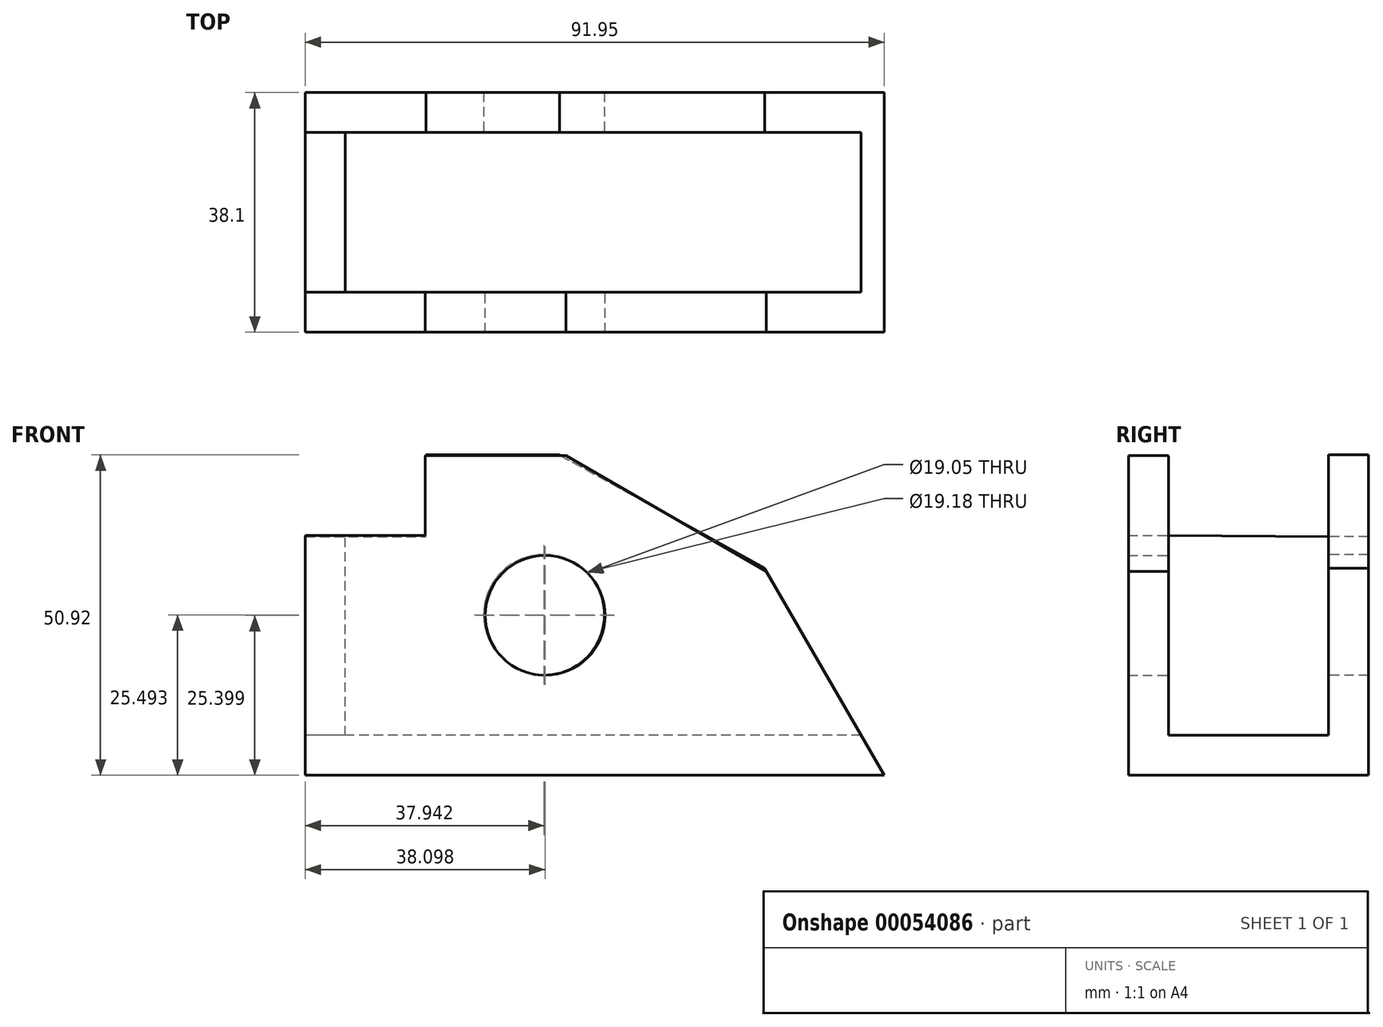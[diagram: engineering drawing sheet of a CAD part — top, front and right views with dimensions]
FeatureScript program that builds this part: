
annotation { "Feature Type Name" : "Feature", "Feature Type Description" : "" }
export const myFeature = defineFeature(function(context is Context, id is Id, definition is map)
    precondition{}
    {
        {
            var Q0;
            Q0=qCreatedBy(makeId("Front.planeOp"),FACE);
            var sketch = newSketch(context, id + "F0", { "sketchPlane" : qUnion([Q0])});
            skLineSegment(sketch, "E0", {"start": v(-65.28, -20.72) * mm, "end": v(26.67, -20.72) * mm});
            skLineSegment(sketch, "E1", {"start": v(-65.28, -20.72) * mm, "end": v(-65.28, 17.38) * mm});
            skLineSegment(sketch, "E2", {"start": v(-65.28, 17.38) * mm, "end": v(-46.23, 17.38) * mm});
            skLineSegment(sketch, "E3", {"start": v(-46.23, 17.38) * mm, "end": v(-46.23, 30.08) * mm});
            skLineSegment(sketch, "E4", {"start": v(-46.23, 30.08) * mm, "end": v(-23.88, 30.08) * mm});
            skLineSegment(sketch, "E5", {"start": v(7.95, 11.7) * mm, "end": v(-23.88, 30.08) * mm});
            skLineSegment(sketch, "E6", {"start": v(7.95, 11.7) * mm, "end": v(26.67, -20.72) * mm});
            skCircle(sketch, "E7", {"center": v(-27.18, 4.68) * mm, "radius": 9.53 * mm});
            skSolve(sketch);
        }
        {
            var Q0;
            Q0 = qSketchRegion(id + "F0", true);
            extrude(context, id + "F1", {"entities" : qUnion([Q0]), "depth" : 6.35 * mm});
        }
        {
            var Q0;
            Q0=makeQuery(id+"F1.opExtrude","CAP_FACE",FACE,{"disambiguationData":[OSD([sQuery(id+"F0.wireOp",EDGE,"E0"),sQuery(id+"F0.wireOp",EDGE,"E1"),sQuery(id+"F0.wireOp",EDGE,"E2"),sQuery(id+"F0.wireOp",EDGE,"E3"),sQuery(id+"F0.wireOp",EDGE,"E4"),sQuery(id+"F0.wireOp",EDGE,"E5"),sQuery(id+"F0.wireOp",EDGE,"E6"),sQuery(id+"F0.wireOp",EDGE,"E7")])],"isStart":true});
            var sketch = newSketch(context, id + "F2", { "sketchPlane" : qUnion([Q0])});
            skLineSegment(sketch, "E8", {"start": v(-26.67, -20.72) * mm, "end": v(-23, -14.37) * mm});
            skLineSegment(sketch, "E9", {"start": v(-23, -14.37) * mm, "end": v(65.28, -14.37) * mm});
            skLineSegment(sketch, "E10", {"start": v(65.28, -14.37) * mm, "end": v(65.28, -20.72) * mm});
            skLineSegment(sketch, "E11", {"start": v(65.28, -20.72) * mm, "end": v(-26.67, -20.72) * mm});
            skSolve(sketch);
        }
        {
            var Q0;
            Q0=makeQuery(id+"F2.imprint","IMPRINT",FACE,{"disambiguationData":[TD([[makeQuery(id+"F2.imprint","IMPRINT",EDGE,{"derivedFrom":sQuery(id+"F2.wireOp",EDGE,"E8")}),1.0]])]});
            extrude(context, id + "F3", {"entities" : qUnion([Q0]), "operationType" : NewBodyOperationType.ADD, "depth" : 25.4 * mm});
        }
        {
            var Q0;
            Q0=makeQuery(id+"F3.opExtrude","CAP_FACE",FACE,{"disambiguationData":[OSD([sQuery(id+"F2.wireOp",EDGE,"E8"),sQuery(id+"F2.wireOp",EDGE,"E9"),sQuery(id+"F2.wireOp",EDGE,"E10"),sQuery(id+"F2.wireOp",EDGE,"E11")])],"isStart":false});
            var sketch = newSketch(context, id + "F4", { "sketchPlane" : qUnion([Q0])});
            skLineSegment(sketch, "E12", {"start": v(-26.67, -20.72) * mm, "end": v(65.28, -20.72) * mm});
            skLineSegment(sketch, "E13", {"start": v(65.28, -20.72) * mm, "end": v(65.28, 17.22) * mm});
            skLineSegment(sketch, "E14", {"start": v(65.28, 17.22) * mm, "end": v(46.1, 17.22) * mm});
            skLineSegment(sketch, "E15", {"start": v(46.1, 17.22) * mm, "end": v(46.1, 30.2) * mm});
            skLineSegment(sketch, "E16", {"start": v(46.1, 30.2) * mm, "end": v(24.9, 30.2) * mm});
            skLineSegment(sketch, "E17", {"start": v(24.9, 30.2) * mm, "end": v(-7.68, 12.18) * mm});
            skLineSegment(sketch, "E18", {"start": v(-7.68, 12.18) * mm, "end": v(-26.67, -20.72) * mm});
            skCircle(sketch, "E19", {"center": v(27.34, 4.77) * mm, "radius": 9.6 * mm});
            skSolve(sketch);
        }
        {
            var Q0;
            Q0 = qSketchRegion(id + "F4", true);
            extrude(context, id + "F5", {"entities" : qUnion([Q0]), "operationType" : NewBodyOperationType.ADD, "depth" : 6.35 * mm});
        }
        {
            var Q0;
            Q0=makeQuery(id+"F5.boolean.opBoolean","MERGE",FACE,{"derivedFrom":[makeQuery(id+"F3.boolean.opBoolean","MERGE",FACE,{"derivedFrom":[makeQuery(id+"F1.opExtrude","SWEPT_FACE",FACE,{"disambiguationData":[OSD([sQuery(id+"F0.wireOp",EDGE,"E1")])]}),makeQuery(id+"F3.opExtrude","SWEPT_FACE",FACE,{"disambiguationData":[OSD([sQuery(id+"F2.wireOp",EDGE,"E10")])]})]}),makeQuery(id+"F5.opExtrude","SWEPT_FACE",FACE,{"disambiguationData":[OSD([sQuery(id+"F4.wireOp",EDGE,"E13")])]})]});
            var sketch = newSketch(context, id + "F6", { "sketchPlane" : qUnion([Q0])});
            skLineSegment(sketch, "E20", {"start": v(-25.4, 17.22) * mm, "end": v(0, 17.38) * mm});
            skLineSegment(sketch, "E21", {"start": v(0, 17.38) * mm, "end": v(0, -14.37) * mm});
            skLineSegment(sketch, "E22", {"start": v(0, -14.37) * mm, "end": v(-25.4, -14.37) * mm});
            skLineSegment(sketch, "E23", {"start": v(-25.4, -14.37) * mm, "end": v(-25.4, 17.22) * mm});
            skSolve(sketch);
        }
        {
            var Q0;
            Q0 = qSketchRegion(id + "F6", true);
            extrude(context, id + "F7", {"entities" : qUnion([Q0]), "oppositeDirection" : true, "depth" : 6.35 * mm});
        }
    });
